# Revit family: Hager-Vector-IP65-syst-NoHosted-BE-fr
name_source: partatom
category: Electrical Equipment
units: mm (PartAtom-declared; Revit-internal decimal feet)

## family parameters
Always vertical = Yes
Cut with Voids When Loaded = No
Panel Configuration = Two Columns, Circuits Across
Part Type = Panelboard
Room Calculation Point = No
Round Connector Dimension = Use Diameter
Shared = No
Work Plane-Based = Yes

## types (1)
- Saillie IP65 L237 H210 P114 10 Modules - VE110M
    Default Elevation = 1219 mm
    EF000003 - mode de pose = EV000384 - saillie
    EF000007 - couleur = EV000270 - gris
    EF000008 - largeur = 237 mm  [stored 0.777559 ft]
    EF000040 - hauteur = 210 mm  [stored 0.688976 ft]
    EF000049 - profondeur = 114 mm  [stored 0.374016 ft]
    EF000116 - numéro RAL = 7035
    EF000118 - avec cadre/support de montage = No
    EF000218 - profondeur d'encastrement = 0 mm  [stored 0 ft]
    EF000266 - nombre de rangées = 1
    EF000332 - hauteur d'encastrement = 0 mm  [stored 0 ft]
    EF000339 - type de capot = EV004216 - porte
    EF000846 - largeur d'encastrement = 0 mm  [stored 0 ft]
    EF001062 - finition CEM = No
    EF001088 - possibilité de montage en saillie = Yes
    EF001131 - profondeur intérieure = 114 mm  [stored 0.374016 ft]
    EF001134 - rail DIN = Yes
    EF001596 - matériau du boîtier/corps = EV000139 - plastique
    EF002950 - largeur en nombre de modules = 10
    EF004462 - type de fermeture = EV000154 - autre
    EF005474 - indice de protection (IP) = EV006421 - IP65
    EF006244 - couvercle/porte transparent(e) = Yes
    EF006306 - avec serrure = No
    EF009212 - finition du couvercle = EV000116 - fermé
    EF015776 - borne de mise à la terre = No
    EF015777 - borne à conducteur neutre = No
    EF015941 - porte pour transmission du signal = Yes
    HG000001 - nombre de colonnes = 1
    HG000002 - avec porte = Yes
    HG000003 - Gamme = Vector
    HG000004 - Référence fabricant = VE110M
    HG000005 - Epaisseur = 3 mm  [stored 0.00984252 ft]
    HG000006 - Encastré = No
    HG000007 - Nombre de colonnes vides = 0
    HG000008 - Nombre de rangées vides = 0
    HG000009 - Porte à double battant = No
    HG000010 - Portes asymétriques = No
    HG000011 - Rangées du bas vides = No
    HG000017 - Distance entre pôles = 18 mm  [stored 0.0590551 ft]
    Manufacturer = Hager
    Model = VE110M
    Type Comments = Vector

note: [stored X ft] marks values corroborated as IEEE doubles in the binary element streams (Revit-internal decimal feet)

## geometry (parser evidence)
native form markers: Sweep x12
no freeform markers — native parametric forms only
